# Revit family: Bicycle Stand Lyra High Extension
name_source: partatom
category: Furniture
units: mm (PartAtom-declared; Revit-internal decimal feet)

## family parameters
Always vertical = Yes
Cut with Voids When Loaded = No
OmniClass Number = 23.21.23.13.15
Room Calculation Point = No
Shared = No
Work Plane-Based = No

## types (2) — shared parameters
BIMobject category = Outdoor Furniture
Body material_90 = Hags - Steel - Powder coated - Gray
Construction material = Hags - Steel - Powder coated - Gray
Description = Bicycle Stand Lyra High Extensionl
Edition number = 1
IFC Classification = Furniture
Manufacturer = Hags
Manufacturer name = HAGS
OmniClass Code = 23-21 23 13 15
OmniClass Description = Furniture
Product name = Bicycle Stand Lyra High Extension
Product url = https://www.hags.com
URL = https://www.hags.com
Uniclass 1.4 Code = L8211
Uniclass 1.4 Description = Furniture
zero-valued in all types: Default Elevation

## per-type parameters (varying)
| type | Body material | Model |
| 8090169 Black | Hags - Steel - Powder coated - Gray | 8090169 |
| 8090171 Grey | Hags - Steel - Powder coated - Black | 8090171 |

## geometry (parser evidence)
native form markers: Sweep x3
no freeform markers — native parametric forms only
